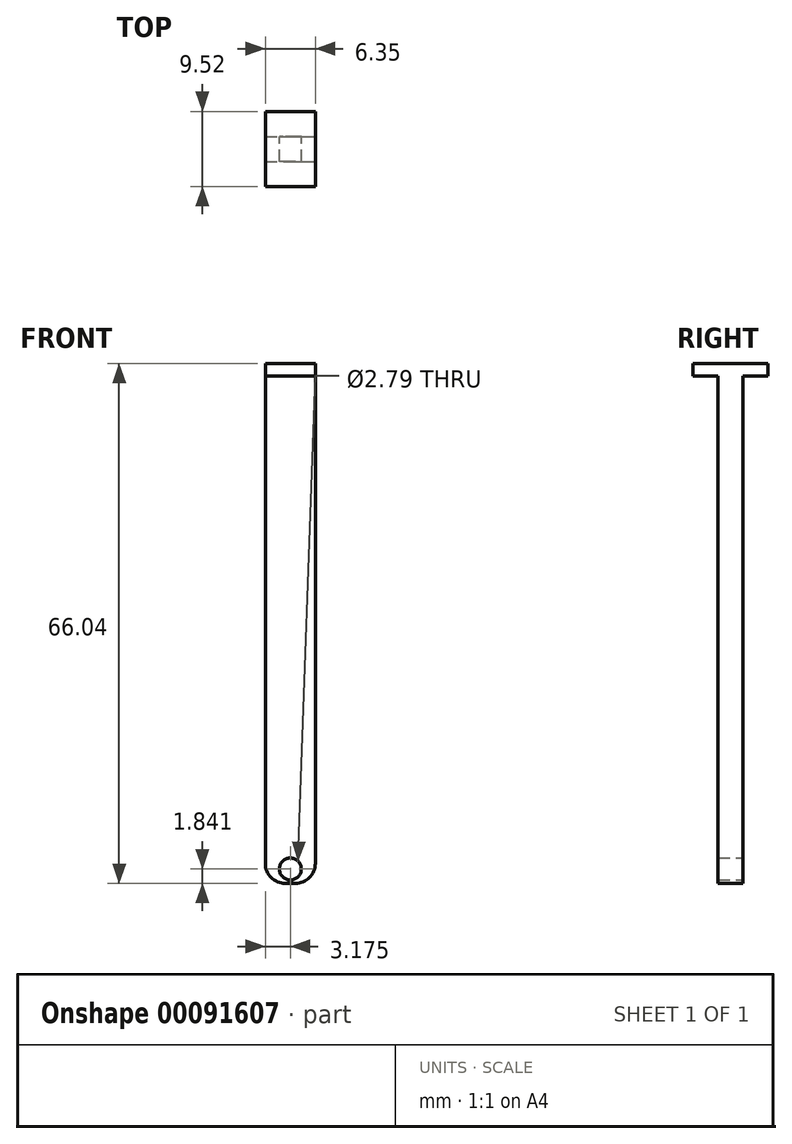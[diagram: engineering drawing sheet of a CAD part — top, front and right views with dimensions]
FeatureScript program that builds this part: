
annotation { "Feature Type Name" : "Feature", "Feature Type Description" : "" }
export const myFeature = defineFeature(function(context is Context, id is Id, definition is map)
    precondition{}
    {
        {
            var Q0;
            Q0=qCreatedBy(makeId("Top.planeOp"),FACE);
            var sketch = newSketch(context, id + "F0", { "sketchPlane" : qUnion([Q0])});
            skLineSegment(sketch, "E0.bottom", {"start": v(0, 0) * mm, "end": v(-6.35, 0) * mm});
            skLineSegment(sketch, "E0.top", {"start": v(0, 3.18) * mm, "end": v(-6.35, 3.18) * mm});
            skLineSegment(sketch, "E0.left", {"start": v(0, 0) * mm, "end": v(0, 3.18) * mm});
            skLineSegment(sketch, "E0.right", {"start": v(-6.35, 0) * mm, "end": v(-6.35, 3.18) * mm});
            skSolve(sketch);
        }
        {
            var Q0;
            Q0 = qSketchRegion(id + "F0", true);
            extrude(context, id + "F1", {"entities" : qUnion([Q0]), "depth" : 66.04 * mm});
        }
        {
            var Q0;
            Q0=makeQuery(id+"F1.opExtrude","SWEPT_FACE",FACE,{"disambiguationData":[OSD([sQuery(id+"F0.wireOp",EDGE,"E0.top")])]});
            var sketch = newSketch(context, id + "F2", { "sketchPlane" : qUnion([Q0])});
            skLineSegment(sketch, "E1.bottom", {"start": v(6.35, 66.04) * mm, "end": v(0, 66.04) * mm});
            skLineSegment(sketch, "E1.top", {"start": v(6.35, 64.45) * mm, "end": v(0, 64.45) * mm});
            skLineSegment(sketch, "E1.left", {"start": v(6.35, 66.04) * mm, "end": v(6.35, 64.45) * mm});
            skLineSegment(sketch, "E1.right", {"start": v(0, 66.04) * mm, "end": v(0, 64.45) * mm});
            skSolve(sketch);
        }
        {
            var Q0;
            Q0 = qSketchRegion(id + "F2", true);
            extrude(context, id + "F3", {"entities" : qUnion([Q0]), "operationType" : NewBodyOperationType.ADD, "depth" : 3.17 * mm, "hasSecondDirection" : true, "secondDirectionOppositeDirection" : true, "secondDirectionDepth" : 6.35 * mm});
        }
        {
            var Q0;
            Q0=makeQuery(id+"F1.opExtrude","SWEPT_FACE",FACE,{"disambiguationData":[OSD([sQuery(id+"F0.wireOp",EDGE,"E0.top")])]});
            var sketch = newSketch(context, id + "F4", { "sketchPlane" : qUnion([Q0])});
            skCircle(sketch, "E2", {"center": v(3.18, 1.84) * mm, "radius": 1.4 * mm});
            skPoint(sketch, "E2.centerSnap0", {"position": v(3.18, 0) * mm});
            skSolve(sketch);
        }
        {
            var Q0;
            Q0 = qSketchRegion(id + "F4", true);
            extrude(context, id + "F5", {"entities" : qUnion([Q0]), "operationType" : NewBodyOperationType.REMOVE, "oppositeDirection" : true, "depth" : 25.4 * mm});
        }
        {
            var Q0;
            Q0=makeQuery(id+"F1.opExtrude","CAP_EDGE",EDGE,{"disambiguationData":[OSD([sQuery(id+"F0.wireOp",EDGE,"E0.right")])],"isStart":true});
            var Q1;
            Q1=makeQuery(id+"F1.opExtrude","CAP_EDGE",EDGE,{"disambiguationData":[OSD([sQuery(id+"F0.wireOp",EDGE,"E0.left")])],"isStart":true});
            fillet(context, id + "F6", {"entities" : qUnion([Q0, Q1]), "radius" : 2.54 * mm, "tangentPropagation" : true, "allowEdgeOverflow" : false});
        }
    });
